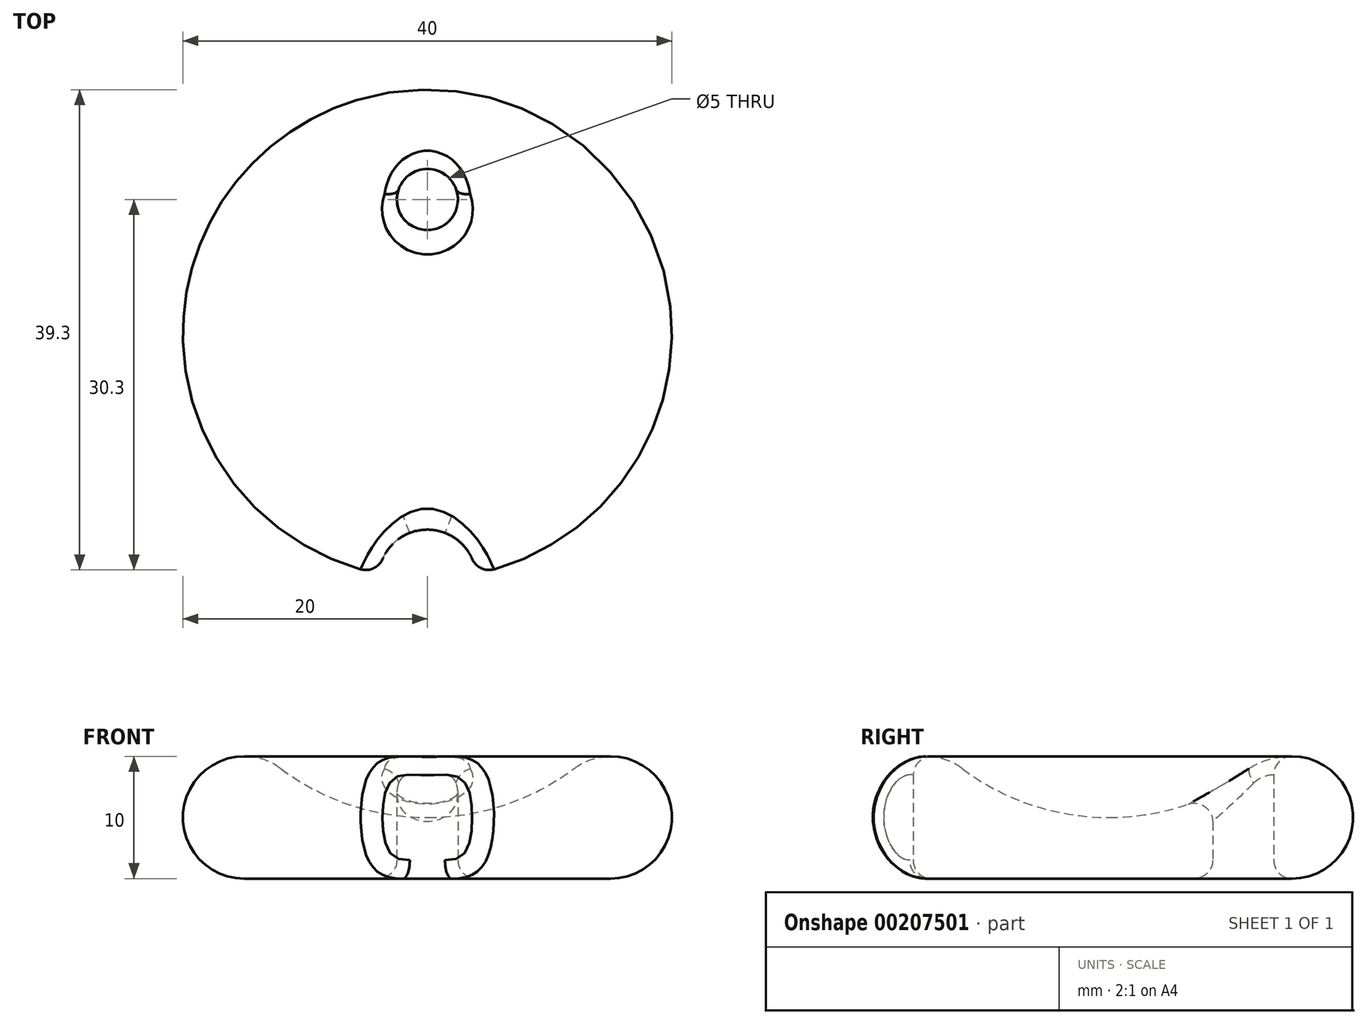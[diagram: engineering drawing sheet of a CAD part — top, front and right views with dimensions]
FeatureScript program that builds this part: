
annotation { "Feature Type Name" : "Feature", "Feature Type Description" : "" }
export const myFeature = defineFeature(function(context is Context, id is Id, definition is map)
    precondition{}
    {
        {
            var Q0;
            Q0=qCreatedBy(makeId("Front.planeOp"),FACE);
            var sketch = newSketch(context, id + "F0", { "sketchPlane" : qUnion([Q0])});
            skArc(sketch, "E0", {"start": v(-12, 9) * mm, "mid": v(-19.74, 6.58) * mm, "end": v(-15, 0) * mm});
            skArc(sketch, "E1", {"start": v(-12, 9) * mm, "mid": v(-6.32, 6.03) * mm, "end": v(0, 5) * mm});
            skLineSegment(sketch, "E2", {"start": v(-15, 0) * mm, "end": v(0, 0) * mm});
            skLineSegment(sketch, "E3", {"start": v(0, 0) * mm, "end": v(0, 5) * mm});
            skSolve(sketch);
        }
        {
            var Q0;
            Q0=qSketchRegion(id+"F0",true);
            var Q1;
            Q1=sQuery(id+"F0.wireOp",EDGE,"E3");
            revolve(context, id + "F1", {"entities" : qUnion([Q0]), "axis" : qUnion([Q1]), "revolveType" : RevolveType.FULL});
        }
        {
            var Q0;
            Q0=qCreatedBy(makeId("Top.planeOp"),FACE);
            var sketch = newSketch(context, id + "F2", { "sketchPlane" : qUnion([Q0])});
            skCircle(sketch, "E4", {"center": v(0, -20) * mm, "radius": 4 * mm});
            skSolve(sketch);
        }
        {
            var Q0;
            Q0=qSketchRegion(id+"F2",true);
            extrude(context, id + "F3", {"entities" : qUnion([Q0]), "operationType" : NewBodyOperationType.REMOVE, "depth" : 11 * mm});
        }
        {
            var Q0;
            Q0=qCreatedBy(makeId("Top.planeOp"),FACE);
            var sketch = newSketch(context, id + "F4", { "sketchPlane" : qUnion([Q0])});
            skCircle(sketch, "E5", {"center": v(0, 11) * mm, "radius": 2.5 * mm});
            skSolve(sketch);
        }
        {
            var Q0;
            Q0=qSketchRegion(id+"F4",true);
            extrude(context, id + "F5", {"entities" : qUnion([Q0]), "operationType" : NewBodyOperationType.REMOVE, "depth" : 10 * mm});
        }
        {
            var Q0;
            Q0=makeQuery(id+"F3.boolean.opBoolean","INTERSECT",EDGE,{"derivedFrom":[makeQuery(id+"FXCRYJaVvK0YUCQ_1.boolean.opBoolean","SPLIT",FACE,{"disambiguationData":[TD([makeQuery(id+"F1.opRevolve","SWEPT_FACE",FACE,{"disambiguationData":[OSD([sQuery(id+"F0.wireOp",EDGE,"E2")])]})])],"derivedFrom":makeQuery(id+"F1.opRevolve","SWEPT_FACE",FACE,{"disambiguationData":[OSD([sQuery(id+"F0.wireOp",EDGE,"E0")])]})}),makeQuery(id+"F3.opExtrude","SWEPT_FACE",FACE,{"disambiguationData":[OSD([sQuery(id+"F2.wireOp",EDGE,"E4")])]})]});
            fillet(context, id + "F6", {"entities" : qUnion([Q0]), "radius" : 1.5 * mm, "tangentPropagation" : true, "allowEdgeOverflow" : false});
        }
        {
            var Q0;
            Q0=makeQuery(id+"F5.boolean.opBoolean","COPY",FACE,{"derivedFrom":makeQuery(id+"F5.opExtrude","SWEPT_FACE",FACE,{"disambiguationData":[OSD([sQuery(id+"F4.wireOp",EDGE,"E5")])]})});
            fillet(context, id + "F7", {"entities" : qUnion([Q0]), "radius" : 1.5 * mm, "tangentPropagation" : true, "allowEdgeOverflow" : false});
        }
    });
